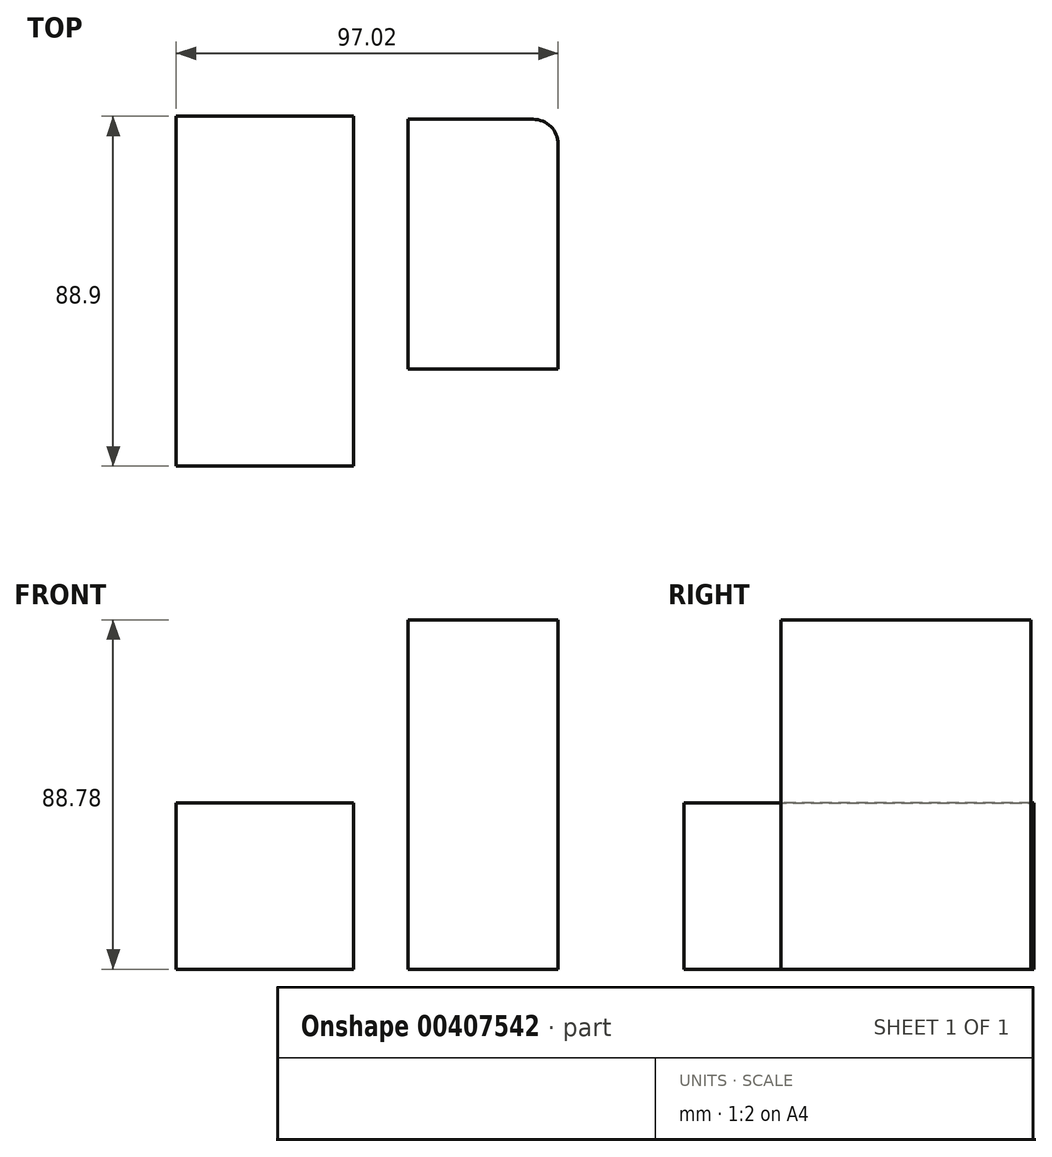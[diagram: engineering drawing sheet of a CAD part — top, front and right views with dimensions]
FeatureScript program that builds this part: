
annotation { "Feature Type Name" : "Feature", "Feature Type Description" : "" }
export const myFeature = defineFeature(function(context is Context, id is Id, definition is map)
    precondition{}
    {
        {
            var Q0;
            Q0=qCreatedBy(makeId("Top.planeOp"),FACE);
            var sketch = newSketch(context, id + "F0", { "sketchPlane" : qUnion([Q0])});
            skLineSegment(sketch, "E0", {"start": v(-33.35, 43.1) * mm, "end": v(11.65, 43.1) * mm});
            skLineSegment(sketch, "E1", {"start": v(11.65, 43.1) * mm, "end": v(11.65, -45.8) * mm});
            skLineSegment(sketch, "E2", {"start": v(11.65, -45.8) * mm, "end": v(-33.35, -45.8) * mm});
            skLineSegment(sketch, "E3", {"start": v(-33.35, -45.8) * mm, "end": v(-33.35, 43.1) * mm});
            skSolve(sketch);
        }
        {
            var Q0;
            Q0 = qSketchRegion(id + "F0", true);
            var sketch = newSketch(context, id + "F1", { "sketchPlane" : qUnion([Q0])});
            skLineSegment(sketch, "E4", {"start": v(25.57, 42.36) * mm, "end": v(57.32, 42.36) * mm});
            skLineSegment(sketch, "E5", {"start": v(63.67, 36.01) * mm, "end": v(63.67, -21.14) * mm});
            skLineSegment(sketch, "E6", {"start": v(63.67, -21.14) * mm, "end": v(25.57, -21.14) * mm});
            skLineSegment(sketch, "E7", {"start": v(25.57, -21.14) * mm, "end": v(25.57, 42.36) * mm});
            skPoint(sketch, "E8.visualSharp", {"position": v(63.67, 42.36) * mm});
            skArc(sketch, "E8.filletArc", {"start": v(63.67, 36.01) * mm, "mid": v(61.8, 40.5) * mm, "end": v(57.32, 42.36) * mm});
            skSolve(sketch);
        }
        {
            var Q0;
            Q0=makeQuery(id+"F1.imprint","IMPRINT",FACE,{"disambiguationData":[TD([[makeQuery(id+"F1.imprint","IMPRINT",EDGE,{"derivedFrom":sQuery(id+"F1.wireOp",EDGE,"E4")}),-1.0]])]});
            extrude(context, id + "F2", {"entities" : qUnion([Q0]), "depth" : 88.78 * mm});
        }
        {
            var Q0;
            Q0=makeQuery(id+"F0.imprint","IMPRINT",FACE,{"disambiguationData":[TD([[makeQuery(id+"F0.imprint","IMPRINT",EDGE,{"derivedFrom":sQuery(id+"F0.wireOp",EDGE,"E0")}),-1.0]])]});
            extrude(context, id + "F3", {"entities" : qUnion([Q0]), "depth" : 42.22 * mm});
        }
    });
